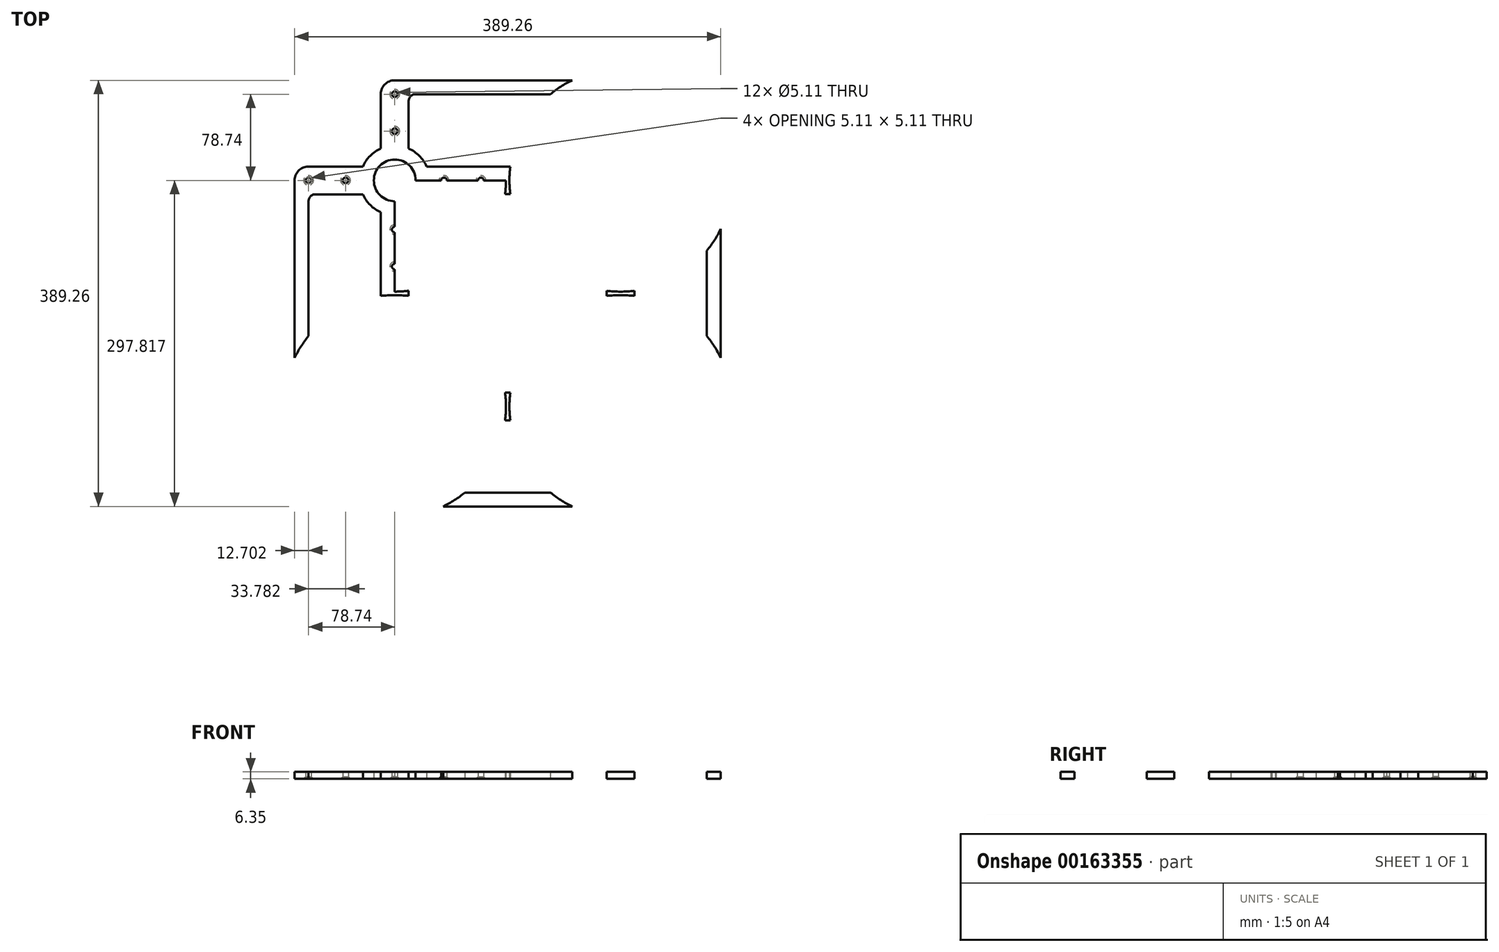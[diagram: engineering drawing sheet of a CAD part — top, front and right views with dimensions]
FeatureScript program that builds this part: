
annotation { "Feature Type Name" : "Feature", "Feature Type Description" : "" }
export const myFeature = defineFeature(function(context is Context, id is Id, definition is map)
    precondition{}
    {
        {
            var Q0;
            Q0=qCreatedBy(makeId("Top.planeOp"),FACE);
            var sketch = newSketch(context, id + "F0", { "sketchPlane" : qUnion([Q0])});
            skLineSegment(sketch, "E0.bottom", {"start": v(103.19, -103.19) * mm, "end": v(-103.19, -103.19) * mm});
            skLineSegment(sketch, "E0.top", {"start": v(103.19, 103.19) * mm, "end": v(-103.19, 103.19) * mm});
            skLineSegment(sketch, "E0.left", {"start": v(103.19, -103.19) * mm, "end": v(103.19, 103.19) * mm});
            skLineSegment(sketch, "E0.right", {"start": v(-103.19, -103.19) * mm, "end": v(-103.19, 90.53) * mm});
            skPoint(sketch, "E0.middle", {"position": v(0, 0) * mm});
            skCircle(sketch, "E1", {"center": v(-103.19, 103.19) * mm, "radius": 101.6 * mm});
            skCircle(sketch, "E2", {"center": v(103.19, 103.19) * mm, "radius": 101.6 * mm});
            skCircle(sketch, "E3", {"center": v(103.19, -103.19) * mm, "radius": 101.6 * mm});
            skCircle(sketch, "E4", {"center": v(-103.19, -103.19) * mm, "radius": 101.6 * mm});
            skLineSegment(sketch, "E5", {"start": v(-103.19, 115.88) * mm, "end": v(-103.19, 148.15) * mm});
            skLineSegment(sketch, "E6", {"start": v(-103.19, 148.15) * mm, "end": v(-103.19, 181.93) * mm});
            skLineSegment(sketch, "E7", {"start": v(-103.19, 103.19) * mm, "end": v(-58.23, 103.19) * mm});
            skLineSegment(sketch, "E8", {"start": v(-58.23, 103.19) * mm, "end": v(-24.45, 103.19) * mm});
            skLineSegment(sketch, "E9", {"start": v(-103.19, 90.53) * mm, "end": v(-103.19, 58.23) * mm});
            skLineSegment(sketch, "E10", {"start": v(-103.19, 58.23) * mm, "end": v(-103.19, 24.45) * mm});
            skLineSegment(sketch, "E11", {"start": v(-103.19, 103.19) * mm, "end": v(-148.15, 103.19) * mm});
            skLineSegment(sketch, "E12", {"start": v(-148.15, 103.19) * mm, "end": v(-181.93, 103.19) * mm});
            skLineSegment(sketch, "E13.MirrorCS", {"start": v(103.19, 103.19) * mm, "end": v(103.19, 58.23) * mm});
            skLineSegment(sketch, "E14.MirrorCS", {"start": v(58.23, 103.19) * mm, "end": v(24.45, 103.19) * mm});
            skLineSegment(sketch, "E15.MirrorCS", {"start": v(103.19, 103.19) * mm, "end": v(58.23, 103.19) * mm});
            skLineSegment(sketch, "E16.MirrorCS", {"start": v(148.15, 103.19) * mm, "end": v(181.93, 103.19) * mm});
            skLineSegment(sketch, "E17.MirrorCS", {"start": v(103.19, 103.19) * mm, "end": v(148.15, 103.19) * mm});
            skLineSegment(sketch, "E18.MirrorCS", {"start": v(103.19, 58.23) * mm, "end": v(103.19, 24.45) * mm});
            skLineSegment(sketch, "E19.MirrorCS", {"start": v(103.19, 103.19) * mm, "end": v(103.19, 148.15) * mm});
            skLineSegment(sketch, "E20.MirrorCS", {"start": v(103.19, 148.15) * mm, "end": v(103.19, 181.93) * mm});
            skLineSegment(sketch, "E21.MirrorCS", {"start": v(-103.19, -103.19) * mm, "end": v(-103.19, -58.23) * mm});
            skLineSegment(sketch, "E22.MirrorCS", {"start": v(-58.23, -103.19) * mm, "end": v(-24.45, -103.19) * mm});
            skLineSegment(sketch, "E23.MirrorCS", {"start": v(-103.19, -103.19) * mm, "end": v(-58.23, -103.19) * mm});
            skLineSegment(sketch, "E24.MirrorCS", {"start": v(-103.19, -148.15) * mm, "end": v(-103.19, -181.93) * mm});
            skLineSegment(sketch, "E25.MirrorCS", {"start": v(-103.19, -103.19) * mm, "end": v(-103.19, -148.15) * mm});
            skLineSegment(sketch, "E26.MirrorCS", {"start": v(-148.15, -103.19) * mm, "end": v(-181.93, -103.19) * mm});
            skLineSegment(sketch, "E27.MirrorCS", {"start": v(-103.19, -103.19) * mm, "end": v(-148.15, -103.19) * mm});
            skLineSegment(sketch, "E28.MirrorCS", {"start": v(-103.19, -58.23) * mm, "end": v(-103.19, -24.45) * mm});
            skLineSegment(sketch, "E29.MirrorCS", {"start": v(148.15, -103.19) * mm, "end": v(181.93, -103.19) * mm});
            skLineSegment(sketch, "E30.MirrorCS", {"start": v(103.19, -103.19) * mm, "end": v(103.19, -58.23) * mm});
            skLineSegment(sketch, "E31.MirrorCS", {"start": v(103.19, -103.19) * mm, "end": v(148.15, -103.19) * mm});
            skLineSegment(sketch, "E32.MirrorCS", {"start": v(103.19, -103.19) * mm, "end": v(58.23, -103.19) * mm});
            skLineSegment(sketch, "E33.MirrorCS", {"start": v(103.19, -58.23) * mm, "end": v(103.19, -24.45) * mm});
            skLineSegment(sketch, "E34.MirrorCS", {"start": v(103.19, -103.19) * mm, "end": v(103.19, -148.15) * mm});
            skLineSegment(sketch, "E35.MirrorCS", {"start": v(58.23, -103.19) * mm, "end": v(24.45, -103.19) * mm});
            skLineSegment(sketch, "E36.MirrorCS", {"start": v(103.19, -148.15) * mm, "end": v(103.19, -181.93) * mm});
            skLineSegment(sketch, "E37", {"start": v(-181.93, 90.49) * mm, "end": v(-181.93, 90.49) * mm});
            skArc(sketch, "E38", {"start": v(-103.19, 194.63) * mm, "mid": v(-112.17, 190.9) * mm, "end": v(-115.89, 181.93) * mm});
            skLineSegment(sketch, "E39", {"start": v(-103.19, 103.19) * mm, "end": v(-115.89, 103.19) * mm});
            skPoint(sketch, "E39.endSnap0", {"position": v(-125.67, 103.19) * mm});
            skLineSegment(sketch, "E40", {"start": v(-115.89, 74.09) * mm, "end": v(-115.89, -2.38) * mm});
            skLineSegment(sketch, "E41", {"start": v(-115.89, -2.38) * mm, "end": v(-115.89, 74.09) * mm});
            skLineSegment(sketch, "E42", {"start": v(-90.52, 175.58) * mm, "end": v(-90.52, 132.3) * mm});
            skLineSegment(sketch, "E43", {"start": v(-182.34, 115.88) * mm, "end": v(-132.29, 115.88) * mm});
            skLineSegment(sketch, "E44.trimOffspring", {"start": v(-2.38, 90.53) * mm, "end": v(2.38, 90.53) * mm});
            skLineSegment(sketch, "E45.trimOffspring", {"start": v(-74.09, 115.88) * mm, "end": v(2.38, 115.88) * mm});
            skLineSegment(sketch, "E46.trimOffspring", {"start": v(-115.89, 132.29) * mm, "end": v(-115.89, 181.93) * mm});
            skPoint(sketch, "E47.visualSharp", {"position": v(-115.89, 115.88) * mm});
            skPoint(sketch, "E48.visualSharp", {"position": v(-90.52, 115.88) * mm});
            skPoint(sketch, "E49.visualSharp", {"position": v(-115.89, 90.53) * mm});
            skPoint(sketch, "E50.visualSharp", {"position": v(-149.1, 90.53) * mm});
            skLineSegment(sketch, "E51", {"start": v(-74.07, 90.53) * mm, "end": v(2.38, 90.53) * mm});
            skLineSegment(sketch, "E52.trimOffspring", {"start": v(-90.52, 74.07) * mm, "end": v(-90.52, -2.38) * mm});
            skPoint(sketch, "E53.visualSharp", {"position": v(-90.52, 90.53) * mm});
            skLineSegment(sketch, "E54", {"start": v(-132.29, 90.49) * mm, "end": v(-175.58, 90.49) * mm});
            skLineSegment(sketch, "E55", {"start": v(-181.93, 84.14) * mm, "end": v(-181.93, -38.98) * mm});
            skLineSegment(sketch, "E56", {"start": v(-181.93, -38.98) * mm, "end": v(-194.63, -38.98) * mm});
            skLineSegment(sketch, "E57", {"start": v(-194.63, -38.98) * mm, "end": v(-194.63, 103.19) * mm});
            skLineSegment(sketch, "E58", {"start": v(-84.17, 181.93) * mm, "end": v(38.98, 181.93) * mm});
            skLineSegment(sketch, "E59", {"start": v(38.98, 181.93) * mm, "end": v(38.98, 194.63) * mm});
            skLineSegment(sketch, "E60", {"start": v(38.98, 194.63) * mm, "end": v(-103.19, 194.63) * mm});
            skArc(sketch, "E61.trimOffspring", {"start": v(-181.52, 115.88) * mm, "mid": v(-190.76, 112.31) * mm, "end": v(-194.63, 103.19) * mm});
            skPoint(sketch, "E62.visualSharp", {"position": v(-181.93, 90.49) * mm});
            skArc(sketch, "E62.filletArc", {"start": v(-175.58, 90.49) * mm, "mid": v(-180.07, 88.63) * mm, "end": v(-181.93, 84.14) * mm});
            skPoint(sketch, "E63.visualSharp", {"position": v(-90.52, 181.93) * mm});
            skArc(sketch, "E63.filletArc", {"start": v(-84.17, 181.93) * mm, "mid": v(-88.66, 180.07) * mm, "end": v(-90.52, 175.58) * mm});
            skLineSegment(sketch, "E64.MirrorCS", {"start": v(90.52, 74.07) * mm, "end": v(90.52, -2.38) * mm});
            skLineSegment(sketch, "E65.MirrorCS", {"start": v(74.07, 90.53) * mm, "end": v(-2.38, 90.53) * mm});
            skLineSegment(sketch, "E66.MirrorCS", {"start": v(74.09, 115.88) * mm, "end": v(-2.38, 115.88) * mm});
            skLineSegment(sketch, "E67.MirrorCS", {"start": v(90.52, 175.58) * mm, "end": v(90.52, 132.3) * mm});
            skLineSegment(sketch, "E68.MirrorCS", {"start": v(115.89, 132.29) * mm, "end": v(115.89, 181.93) * mm});
            skLineSegment(sketch, "E69.MirrorCS", {"start": v(115.89, -2.38) * mm, "end": v(115.89, 74.09) * mm});
            skLineSegment(sketch, "E70.MirrorCS", {"start": v(132.29, 90.49) * mm, "end": v(175.58, 90.49) * mm});
            skLineSegment(sketch, "E71.MirrorCS", {"start": v(182.34, 115.88) * mm, "end": v(132.29, 115.88) * mm});
            skArc(sketch, "E72.MirrorCS", {"start": v(175.58, 90.49) * mm, "mid": v(180.07, 88.63) * mm, "end": v(181.93, 84.14) * mm});
            skLineSegment(sketch, "E73.MirrorCS", {"start": v(181.93, 84.14) * mm, "end": v(181.93, -38.98) * mm});
            skLineSegment(sketch, "E74.MirrorCS", {"start": v(194.63, -38.98) * mm, "end": v(194.63, 103.19) * mm});
            skArc(sketch, "E75.MirrorCS", {"start": v(181.52, 115.88) * mm, "mid": v(190.76, 112.31) * mm, "end": v(194.63, 103.19) * mm});
            skLineSegment(sketch, "E76.MirrorCS", {"start": v(-38.98, 194.63) * mm, "end": v(103.19, 194.63) * mm});
            skLineSegment(sketch, "E77.MirrorCS", {"start": v(84.17, 181.93) * mm, "end": v(-38.98, 181.93) * mm});
            skArc(sketch, "E78.MirrorCS", {"start": v(84.17, 181.93) * mm, "mid": v(88.66, 180.07) * mm, "end": v(90.52, 175.58) * mm});
            skArc(sketch, "E79.MirrorCS", {"start": v(103.19, 194.63) * mm, "mid": v(112.17, 190.9) * mm, "end": v(115.89, 181.93) * mm});
            skLineSegment(sketch, "E80.MirrorCS", {"start": v(-182.34, -115.88) * mm, "end": v(-132.29, -115.88) * mm});
            skArc(sketch, "E81.MirrorCS", {"start": v(-181.52, -115.88) * mm, "mid": v(-190.76, -112.31) * mm, "end": v(-194.63, -103.19) * mm});
            skLineSegment(sketch, "E82.MirrorCS", {"start": v(-194.63, 38.98) * mm, "end": v(-194.63, -103.19) * mm});
            skLineSegment(sketch, "E83.MirrorCS", {"start": v(-181.93, -84.14) * mm, "end": v(-181.93, 38.98) * mm});
            skArc(sketch, "E84.MirrorCS", {"start": v(-175.58, -90.49) * mm, "mid": v(-180.07, -88.63) * mm, "end": v(-181.93, -84.14) * mm});
            skLineSegment(sketch, "E85.MirrorCS", {"start": v(-132.29, -90.49) * mm, "end": v(-175.58, -90.49) * mm});
            skLineSegment(sketch, "E86.MirrorCS", {"start": v(-115.89, 2.38) * mm, "end": v(-115.89, -74.09) * mm});
            skLineSegment(sketch, "E87.MirrorCS", {"start": v(-90.52, -74.07) * mm, "end": v(-90.52, 2.38) * mm});
            skLineSegment(sketch, "E88.MirrorCS", {"start": v(-74.07, -90.53) * mm, "end": v(2.38, -90.53) * mm});
            skLineSegment(sketch, "E89.MirrorCS", {"start": v(-74.09, -115.88) * mm, "end": v(2.38, -115.88) * mm});
            skLineSegment(sketch, "E90.MirrorCS", {"start": v(-90.52, -175.58) * mm, "end": v(-90.52, -132.3) * mm});
            skLineSegment(sketch, "E91.MirrorCS", {"start": v(-115.89, -132.29) * mm, "end": v(-115.89, -181.93) * mm});
            skArc(sketch, "E92.MirrorCS", {"start": v(-103.19, -194.63) * mm, "mid": v(-112.17, -190.9) * mm, "end": v(-115.89, -181.93) * mm});
            skLineSegment(sketch, "E93.MirrorCS", {"start": v(38.98, -194.63) * mm, "end": v(-103.19, -194.63) * mm});
            skLineSegment(sketch, "E94.MirrorCS", {"start": v(-84.17, -181.93) * mm, "end": v(38.98, -181.93) * mm});
            skArc(sketch, "E95.MirrorCS", {"start": v(-84.17, -181.93) * mm, "mid": v(-88.66, -180.07) * mm, "end": v(-90.52, -175.58) * mm});
            skLineSegment(sketch, "E96.MirrorCS", {"start": v(115.89, -132.29) * mm, "end": v(115.89, -181.93) * mm});
            skArc(sketch, "E97.MirrorCS", {"start": v(103.19, -194.63) * mm, "mid": v(112.17, -190.9) * mm, "end": v(115.89, -181.93) * mm});
            skArc(sketch, "E98.MirrorCS", {"start": v(84.17, -181.93) * mm, "mid": v(88.66, -180.07) * mm, "end": v(90.52, -175.58) * mm});
            skLineSegment(sketch, "E99.MirrorCS", {"start": v(90.52, -175.58) * mm, "end": v(90.52, -132.3) * mm});
            skLineSegment(sketch, "E100.MirrorCS", {"start": v(74.07, -90.53) * mm, "end": v(-2.38, -90.53) * mm});
            skLineSegment(sketch, "E101.MirrorCS", {"start": v(74.09, -115.88) * mm, "end": v(-2.38, -115.88) * mm});
            skLineSegment(sketch, "E102.MirrorCS", {"start": v(90.52, -74.07) * mm, "end": v(90.52, 2.38) * mm});
            skLineSegment(sketch, "E103.MirrorCS", {"start": v(132.29, -90.49) * mm, "end": v(175.58, -90.49) * mm});
            skArc(sketch, "E104.MirrorCS", {"start": v(175.58, -90.49) * mm, "mid": v(180.07, -88.63) * mm, "end": v(181.93, -84.14) * mm});
            skArc(sketch, "E105.MirrorCS", {"start": v(181.52, -115.88) * mm, "mid": v(190.76, -112.31) * mm, "end": v(194.63, -103.19) * mm});
            skLineSegment(sketch, "E106.MirrorCS", {"start": v(194.63, 38.98) * mm, "end": v(194.63, -103.19) * mm});
            skLineSegment(sketch, "E107.MirrorCS", {"start": v(181.93, -84.14) * mm, "end": v(181.93, 38.98) * mm});
            skLineSegment(sketch, "E108.MirrorCS", {"start": v(182.34, -115.88) * mm, "end": v(132.29, -115.88) * mm});
            skLineSegment(sketch, "E109.MirrorCS", {"start": v(-38.98, -194.63) * mm, "end": v(103.19, -194.63) * mm});
            skLineSegment(sketch, "E110.MirrorCS", {"start": v(84.17, -181.93) * mm, "end": v(-38.98, -181.93) * mm});
            skLineSegment(sketch, "E111.MirrorCS", {"start": v(115.89, 2.38) * mm, "end": v(115.89, -74.09) * mm});
            skCircle(sketch, "E112", {"center": v(-103.19, 103.19) * mm, "radius": 19.05 * mm});
            skArc(sketch, "E113", {"start": v(-132.29, 90.49) * mm, "mid": v(-125.64, 80.74) * mm, "end": v(-115.89, 74.09) * mm});
            skCircle(sketch, "E114", {"center": v(103.19, 103.19) * mm, "radius": 19.05 * mm});
            skArc(sketch, "E115", {"start": v(74.07, 90.53) * mm, "mid": v(80.73, 80.74) * mm, "end": v(90.52, 74.07) * mm});
            skCircle(sketch, "E116", {"center": v(-103.19, -103.19) * mm, "radius": 19.05 * mm});
            skArc(sketch, "E117", {"start": v(-132.29, -115.88) * mm, "mid": v(-125.64, -125.64) * mm, "end": v(-115.89, -132.29) * mm});
            skArc(sketch, "E118", {"start": v(74.09, -115.88) * mm, "mid": v(80.75, -125.65) * mm, "end": v(90.52, -132.3) * mm});
            skPoint(sketch, "E47.filletArc.start.orphan", {"position": v(-122.24, 115.88) * mm});
            skPoint(sketch, "E119.orphan", {"position": v(-115.89, 122.23) * mm});
            skPoint(sketch, "E48.filletArc.start.orphan", {"position": v(-90.52, 122.23) * mm});
            skPoint(sketch, "E120.orphan", {"position": v(-84.17, 115.88) * mm});
            skPoint(sketch, "E53.filletArc.start.orphan", {"position": v(-84.17, 90.53) * mm});
            skPoint(sketch, "E121.orphan", {"position": v(-90.52, 84.18) * mm});
            skPoint(sketch, "E122.orphan", {"position": v(-121.7, 90.49) * mm});
            skArc(sketch, "E123.trimOffspring", {"start": v(-115.89, 132.29) * mm, "mid": v(-125.64, 125.64) * mm, "end": v(-132.29, 115.88) * mm});
            skArc(sketch, "E124.trimOffspring", {"start": v(-74.09, 115.88) * mm, "mid": v(-80.75, 125.65) * mm, "end": v(-90.52, 132.3) * mm});
            skArc(sketch, "E125.trimOffspring", {"start": v(-90.52, 74.07) * mm, "mid": v(-80.73, 80.74) * mm, "end": v(-74.07, 90.53) * mm});
            skPoint(sketch, "E126.orphan", {"position": v(-115.89, 84.16) * mm});
            skPoint(sketch, "E127.orphan", {"position": v(90.52, 122.23) * mm});
            skPoint(sketch, "E128.MirrorCS.end.orphan", {"position": v(84.17, 115.88) * mm});
            skPoint(sketch, "E129.orphan", {"position": v(115.89, 122.23) * mm});
            skPoint(sketch, "E130.MirrorCS.start.orphan", {"position": v(122.24, 115.88) * mm});
            skPoint(sketch, "E131.orphan", {"position": v(121.7, 90.49) * mm});
            skPoint(sketch, "E132.orphan", {"position": v(115.89, 84.16) * mm});
            skPoint(sketch, "E133.orphan", {"position": v(84.17, 90.53) * mm});
            skPoint(sketch, "E134.MirrorCS.end.orphan", {"position": v(90.52, 84.18) * mm});
            skArc(sketch, "E135.trimOffspring", {"start": v(90.52, 132.3) * mm, "mid": v(80.75, 125.65) * mm, "end": v(74.09, 115.88) * mm});
            skArc(sketch, "E136.trimOffspring", {"start": v(132.29, 115.88) * mm, "mid": v(125.64, 125.64) * mm, "end": v(115.89, 132.29) * mm});
            skArc(sketch, "E137.trimOffspring", {"start": v(115.89, 74.09) * mm, "mid": v(125.64, 80.74) * mm, "end": v(132.29, 90.49) * mm});
            skPoint(sketch, "E138.orphan", {"position": v(90.52, -84.18) * mm});
            skPoint(sketch, "E139.orphan", {"position": v(84.17, -90.53) * mm});
            skPoint(sketch, "E140.orphan", {"position": v(115.89, -84.16) * mm});
            skPoint(sketch, "E141.MirrorCS.end.orphan", {"position": v(121.7, -90.49) * mm});
            skPoint(sketch, "E142.orphan", {"position": v(122.24, -115.88) * mm});
            skPoint(sketch, "E143.MirrorCS.end.orphan", {"position": v(115.89, -122.23) * mm});
            skPoint(sketch, "E144.MirrorCS.end.orphan", {"position": v(84.17, -115.88) * mm});
            skPoint(sketch, "E144.MirrorCS.start.orphan", {"position": v(90.52, -122.23) * mm});
            skArc(sketch, "E145.trimOffspring", {"start": v(90.52, -74.07) * mm, "mid": v(80.73, -80.74) * mm, "end": v(74.07, -90.53) * mm});
            skArc(sketch, "E146.trimOffspring", {"start": v(132.29, -90.49) * mm, "mid": v(125.64, -80.74) * mm, "end": v(115.89, -74.09) * mm});
            skArc(sketch, "E147.trimOffspring", {"start": v(115.89, -132.29) * mm, "mid": v(125.64, -125.64) * mm, "end": v(132.29, -115.88) * mm});
            skCircle(sketch, "E148", {"center": v(103.19, -103.19) * mm, "radius": 19.05 * mm});
            skPoint(sketch, "E149.orphan", {"position": v(-121.7, -90.49) * mm});
            skPoint(sketch, "E150.orphan", {"position": v(-115.89, -84.16) * mm});
            skArc(sketch, "E151.trimOffspring", {"start": v(-115.89, -74.09) * mm, "mid": v(-125.64, -80.74) * mm, "end": v(-132.29, -90.49) * mm});
            skPoint(sketch, "E152.orphan", {"position": v(-90.52, -84.18) * mm});
            skPoint(sketch, "E153.MirrorCS.start.orphan", {"position": v(-84.17, -90.53) * mm});
            skArc(sketch, "E154.trimOffspring", {"start": v(-74.07, -90.53) * mm, "mid": v(-80.73, -80.74) * mm, "end": v(-90.52, -74.07) * mm});
            skPoint(sketch, "E155.orphan", {"position": v(-84.17, -115.88) * mm});
            skPoint(sketch, "E156.MirrorCS.start.orphan", {"position": v(-90.52, -122.23) * mm});
            skArc(sketch, "E157.trimOffspring", {"start": v(-90.52, -132.3) * mm, "mid": v(-80.75, -125.65) * mm, "end": v(-74.09, -115.88) * mm});
            skPoint(sketch, "E158.orphan", {"position": v(-115.89, -122.23) * mm});
            skPoint(sketch, "E159.MirrorCS.start.orphan", {"position": v(-122.24, -115.88) * mm});
            skSolve(sketch);
        }
        {
            var Q0;
            {var subQ8=sQuery(id+"F0.wireOp",EDGE,"E14.MirrorCS");Q0=makeQuery(id+"F0.imprint","IMPRINT",FACE,{"disambiguationData":[TD([[makeQuery(id+"F0.imprint","IMPRINT",EDGE,{"derivedFrom":subQ8}),-1.0]])]});}
            var Q1;
            {var subQ1=sQuery(id+"F0.wireOp",EDGE,"E14.MirrorCS");Q1=makeQuery(id+"F0.imprint","IMPRINT",FACE,{"disambiguationData":[TD([[makeQuery(id+"F0.imprint","IMPRINT",EDGE,{"derivedFrom":subQ1}),1.0]])]});}
            var Q2;
            {var subQ0=sQuery(id+"F0.wireOp",EDGE,"E106.MirrorCS");var subQ3=sQuery(id+"F0.wireOp",EDGE,"E3");var subQ4=makeQuery(id+"F0.imprint","INTERSECT",VERTEX,{"derivedFrom":[subQ3,subQ0]});Q2=makeQuery(id+"F0.imprint","IMPRINT",FACE,{"disambiguationData":[TD([[makeQuery(id+"F0.imprint","IMPRINT",EDGE,{"disambiguationData":[TD([[subQ4,-1.0]])],"derivedFrom":subQ3}),-1.0]])]});}
            var Q3;
            {var subQ0=sQuery(id+"F0.wireOp",EDGE,"E3");var subQ1=sQuery(id+"F0.wireOp",EDGE,"E0.left");var subQ2=makeQuery(id+"F0.imprint","INTERSECT",VERTEX,{"derivedFrom":[subQ1,subQ0]});Q3=makeQuery(id+"F0.imprint","IMPRINT",FACE,{"disambiguationData":[TD([[makeQuery(id+"F0.imprint","IMPRINT",EDGE,{"disambiguationData":[TD([[subQ2,-1.0]])],"derivedFrom":subQ1}),1.0]])]});}
            var Q4;
            {var subQ0=sQuery(id+"F0.wireOp",EDGE,"E3");var subQ1=sQuery(id+"F0.wireOp",EDGE,"E0.left");var subQ2=makeQuery(id+"F0.imprint","INTERSECT",VERTEX,{"derivedFrom":[subQ1,subQ0]});Q4=makeQuery(id+"F0.imprint","IMPRINT",FACE,{"disambiguationData":[TD([[makeQuery(id+"F0.imprint","IMPRINT",EDGE,{"disambiguationData":[TD([[subQ2,-1.0]])],"derivedFrom":subQ1}),-1.0]])]});}
            var Q5;
            {var subQ0=sQuery(id+"F0.wireOp",EDGE,"E109.MirrorCS");var subQ3=sQuery(id+"F0.wireOp",EDGE,"E3");var subQ4=makeQuery(id+"F0.imprint","INTERSECT",VERTEX,{"derivedFrom":[subQ3,subQ0]});Q5=makeQuery(id+"F0.imprint","IMPRINT",FACE,{"disambiguationData":[TD([[makeQuery(id+"F0.imprint","IMPRINT",EDGE,{"disambiguationData":[TD([[subQ4,1.0]])],"derivedFrom":subQ3}),-1.0]])]});}
            var Q6;
            {var subQ0=sQuery(id+"F0.wireOp",EDGE,"E3");var subQ1=sQuery(id+"F0.wireOp",EDGE,"E0.bottom");var subQ2=makeQuery(id+"F0.imprint","INTERSECT",VERTEX,{"derivedFrom":[subQ1,subQ0]});Q6=makeQuery(id+"F0.imprint","IMPRINT",FACE,{"disambiguationData":[TD([[makeQuery(id+"F0.imprint","IMPRINT",EDGE,{"disambiguationData":[TD([[subQ2,-1.0]])],"derivedFrom":subQ1}),-1.0]])]});}
            var Q7;
            {var subQ0=sQuery(id+"F0.wireOp",EDGE,"E3");var subQ1=sQuery(id+"F0.wireOp",EDGE,"E0.bottom");var subQ2=makeQuery(id+"F0.imprint","INTERSECT",VERTEX,{"derivedFrom":[subQ1,subQ0]});Q7=makeQuery(id+"F0.imprint","IMPRINT",FACE,{"disambiguationData":[TD([[makeQuery(id+"F0.imprint","IMPRINT",EDGE,{"disambiguationData":[TD([[subQ2,-1.0]])],"derivedFrom":subQ1}),1.0]])]});}
            var Q8;
            {var subQ0=sQuery(id+"F0.wireOp",EDGE,"E56");Q8=makeQuery(id+"F0.imprint","IMPRINT",FACE,{"disambiguationData":[TD([[makeQuery(id+"F0.imprint","IMPRINT",EDGE,{"derivedFrom":subQ0}),1.0]])]});}
            var Q9;
            {var subQ1=sQuery(id+"F0.wireOp",EDGE,"E56");Q9=makeQuery(id+"F0.imprint","IMPRINT",FACE,{"disambiguationData":[TD([[makeQuery(id+"F0.imprint","IMPRINT",EDGE,{"derivedFrom":subQ1}),-1.0]])]});}
            var Q10;
            {var subQ17=sQuery(id+"F0.wireOp",EDGE,"E38");Q10=makeQuery(id+"F0.imprint","IMPRINT",FACE,{"disambiguationData":[TD([[makeQuery(id+"F0.imprint","IMPRINT",EDGE,{"derivedFrom":subQ17}),1.0]])]});}
            var Q11;
            {var subQ0=sQuery(id+"F0.wireOp",EDGE,"E1");var subQ1=sQuery(id+"F0.wireOp",EDGE,"E0.right");var subQ2=makeQuery(id+"F0.imprint","INTERSECT",VERTEX,{"derivedFrom":[subQ1,subQ0]});Q11=makeQuery(id+"F0.imprint","IMPRINT",FACE,{"disambiguationData":[TD([[makeQuery(id+"F0.imprint","IMPRINT",EDGE,{"disambiguationData":[TD([[subQ2,1.0]])],"derivedFrom":subQ1}),1.0]])]});}
            var Q12;
            {var subQ0=sQuery(id+"F0.wireOp",EDGE,"E1");var subQ1=sQuery(id+"F0.wireOp",EDGE,"E0.right");var subQ2=makeQuery(id+"F0.imprint","INTERSECT",VERTEX,{"derivedFrom":[subQ1,subQ0]});Q12=makeQuery(id+"F0.imprint","IMPRINT",FACE,{"disambiguationData":[TD([[makeQuery(id+"F0.imprint","IMPRINT",EDGE,{"disambiguationData":[TD([[subQ2,1.0]])],"derivedFrom":subQ1}),-1.0]])]});}
            var Q13;
            {var subQ0=sQuery(id+"F0.wireOp",EDGE,"E1");var subQ1=sQuery(id+"F0.wireOp",EDGE,"E0.top");var subQ2=makeQuery(id+"F0.imprint","INTERSECT",VERTEX,{"derivedFrom":[subQ1,subQ0]});Q13=makeQuery(id+"F0.imprint","IMPRINT",FACE,{"disambiguationData":[TD([[makeQuery(id+"F0.imprint","IMPRINT",EDGE,{"disambiguationData":[TD([[subQ2,1.0]])],"derivedFrom":subQ1}),1.0]])]});}
            var Q14;
            {var subQ0=sQuery(id+"F0.wireOp",EDGE,"E1");var subQ1=sQuery(id+"F0.wireOp",EDGE,"E0.top");var subQ2=makeQuery(id+"F0.imprint","INTERSECT",VERTEX,{"derivedFrom":[subQ1,subQ0]});Q14=makeQuery(id+"F0.imprint","IMPRINT",FACE,{"disambiguationData":[TD([[makeQuery(id+"F0.imprint","IMPRINT",EDGE,{"disambiguationData":[TD([[subQ2,1.0]])],"derivedFrom":subQ1}),-1.0]])]});}
            var Q15;
            {var subQ1=sQuery(id+"F0.wireOp",EDGE,"E59");Q15=makeQuery(id+"F0.imprint","IMPRINT",FACE,{"disambiguationData":[TD([[makeQuery(id+"F0.imprint","IMPRINT",EDGE,{"derivedFrom":subQ1}),1.0]])]});}
            var Q16;
            {var subQ0=sQuery(id+"F0.wireOp",EDGE,"E59");Q16=makeQuery(id+"F0.imprint","IMPRINT",FACE,{"disambiguationData":[TD([[makeQuery(id+"F0.imprint","IMPRINT",EDGE,{"derivedFrom":subQ0}),-1.0]])]});}
            var Q17;
            {var subQ2=sQuery(id+"F0.wireOp",EDGE,"E8");Q17=makeQuery(id+"F0.imprint","IMPRINT",FACE,{"disambiguationData":[TD([[makeQuery(id+"F0.imprint","IMPRINT",EDGE,{"derivedFrom":subQ2}),-1.0]])]});}
            var Q18;
            {var subQ7=sQuery(id+"F0.wireOp",EDGE,"E33.MirrorCS");Q18=makeQuery(id+"F0.imprint","IMPRINT",FACE,{"disambiguationData":[TD([[makeQuery(id+"F0.imprint","IMPRINT",EDGE,{"derivedFrom":subQ7}),1.0]])]});}
            var Q19;
            {var subQ30=sQuery(id+"F0.wireOp",EDGE,"E33.MirrorCS");Q19=makeQuery(id+"F0.imprint","IMPRINT",FACE,{"disambiguationData":[TD([[makeQuery(id+"F0.imprint","IMPRINT",EDGE,{"derivedFrom":subQ30}),-1.0]])]});}
            var Q20;
            {var subQ5=sQuery(id+"F0.wireOp",EDGE,"E22.MirrorCS");Q20=makeQuery(id+"F0.imprint","IMPRINT",FACE,{"disambiguationData":[TD([[makeQuery(id+"F0.imprint","IMPRINT",EDGE,{"derivedFrom":subQ5}),1.0]])]});}
            var Q21;
            {var subQ21=sQuery(id+"F0.wireOp",EDGE,"E22.MirrorCS");Q21=makeQuery(id+"F0.imprint","IMPRINT",FACE,{"disambiguationData":[TD([[makeQuery(id+"F0.imprint","IMPRINT",EDGE,{"derivedFrom":subQ21}),-1.0]])]});}
            extrude(context, id + "F1", {"entities" : qUnion([Q0, Q1, Q2, Q3, Q4, Q5, Q6, Q7, Q8, Q9, Q10, Q11, Q12, Q13, Q14, Q15, Q16, Q17, Q18, Q19, Q20, Q21]), "depth" : 6.35 * mm});
        }
        {
            var Q0;
            Q0=sQuery(id+"F0.wireOp",VERTEX,"E6.end");
            var Q1;
            Q1=sQuery(id+"F0.wireOp",VERTEX,"E6.start");
            var Q2;
            Q2=sQuery(id+"F0.wireOp",VERTEX,"E10.start");
            var Q3;
            Q3=sQuery(id+"F0.wireOp",VERTEX,"E10.end");
            var Q4;
            Q4=sQuery(id+"F0.wireOp",VERTEX,"E8.start");
            var Q5;
            Q5=sQuery(id+"F0.wireOp",VERTEX,"E8.end");
            var Q6;
            Q6=sQuery(id+"F0.wireOp",VERTEX,"E12.start");
            var Q7;
            Q7=sQuery(id+"F0.wireOp",VERTEX,"E81.MirrorCS.center");
            var Q8;
            Q8=sQuery(id+"F0.wireOp",VERTEX,"E27.MirrorCS.end");
            var Q9;
            Q9=sQuery(id+"F0.wireOp",VERTEX,"E21.MirrorCS.end");
            var Q10;
            Q10=sQuery(id+"F0.wireOp",VERTEX,"E28.MirrorCS.end");
            var Q11;
            Q11=sQuery(id+"F0.wireOp",VERTEX,"E22.MirrorCS.start");
            var Q12;
            Q12=sQuery(id+"F0.wireOp",VERTEX,"E22.MirrorCS.end");
            var Q13;
            Q13=sQuery(id+"F0.wireOp",VERTEX,"E25.MirrorCS.end");
            var Q14;
            Q14=sQuery(id+"F0.wireOp",VERTEX,"E92.MirrorCS.center");
            var Q15;
            Q15=sQuery(id+"F0.wireOp",VERTEX,"E14.MirrorCS.end");
            var Q16;
            Q16=sQuery(id+"F0.wireOp",VERTEX,"E15.MirrorCS.end");
            var Q17;
            Q17=sQuery(id+"F0.wireOp",VERTEX,"E79.MirrorCS.center");
            var Q18;
            Q18=sQuery(id+"F0.wireOp",VERTEX,"E20.MirrorCS.start");
            var Q19;
            Q19=sQuery(id+"F0.wireOp",VERTEX,"E13.MirrorCS.end");
            var Q20;
            Q20=sQuery(id+"F0.wireOp",VERTEX,"E18.MirrorCS.end");
            var Q21;
            Q21=sQuery(id+"F0.wireOp",VERTEX,"E33.MirrorCS.end");
            var Q22;
            Q22=sQuery(id+"F0.wireOp",VERTEX,"E30.MirrorCS.end");
            var Q23;
            Q23=sQuery(id+"F0.wireOp",VERTEX,"E36.MirrorCS.start");
            var Q24;
            Q24=sQuery(id+"F0.wireOp",VERTEX,"E36.MirrorCS.end");
            var Q25;
            Q25=sQuery(id+"F0.wireOp",VERTEX,"E35.MirrorCS.start");
            var Q26;
            Q26=sQuery(id+"F0.wireOp",VERTEX,"E35.MirrorCS.end");
            var Q27;
            Q27=sQuery(id+"F0.wireOp",VERTEX,"E17.MirrorCS.end");
            var Q28;
            Q28=sQuery(id+"F0.wireOp",VERTEX,"E16.MirrorCS.end");
            var Q29;
            Q29=sQuery(id+"F0.wireOp",VERTEX,"E29.MirrorCS.end");
            var Q30;
            Q30=sQuery(id+"F0.wireOp",VERTEX,"E29.MirrorCS.start");
            var Q31;
            Q31=makeQuery(id+"F1.opExtrude","SWEPT_BODY",BODY,{"disambiguationData":[OSD([sQuery(id+"F0.wireOp",EDGE,"E38"),sQuery(id+"F0.wireOp",EDGE,"E41"),sQuery(id+"F0.wireOp",EDGE,"E42"),sQuery(id+"F0.wireOp",EDGE,"E43"),sQuery(id+"F0.wireOp",EDGE,"E45.trimOffspring"),sQuery(id+"F0.wireOp",EDGE,"E46.trimOffspring"),sQuery(id+"F0.wireOp",EDGE,"E47.filletArc"),sQuery(id+"F0.wireOp",EDGE,"E48.filletArc"),sQuery(id+"F0.wireOp",EDGE,"E49.filletArc"),sQuery(id+"F0.wireOp",EDGE,"E51"),sQuery(id+"F0.wireOp",EDGE,"E52.trimOffspring"),sQuery(id+"F0.wireOp",EDGE,"E53.filletArc"),sQuery(id+"F0.wireOp",EDGE,"E54"),sQuery(id+"F0.wireOp",EDGE,"E55"),sQuery(id+"F0.wireOp",EDGE,"E57"),sQuery(id+"F0.wireOp",EDGE,"E58"),sQuery(id+"F0.wireOp",EDGE,"E60"),sQuery(id+"F0.wireOp",EDGE,"E61.trimOffspring"),sQuery(id+"F0.wireOp",EDGE,"E62.filletArc"),sQuery(id+"F0.wireOp",EDGE,"E63.filletArc"),sQuery(id+"F0.wireOp",EDGE,"E64.MirrorCS"),sQuery(id+"F0.wireOp",EDGE,"E65.MirrorCS"),sQuery(id+"F0.wireOp",EDGE,"E134.MirrorCS"),sQuery(id+"F0.wireOp",EDGE,"E128.MirrorCS"),sQuery(id+"F0.wireOp",EDGE,"E66.MirrorCS"),sQuery(id+"F0.wireOp",EDGE,"E67.MirrorCS"),sQuery(id+"F0.wireOp",EDGE,"E130.MirrorCS"),sQuery(id+"F0.wireOp",EDGE,"E68.MirrorCS"),sQuery(id+"F0.wireOp",EDGE,"221127f1-edb8-49a0-b02f-fde569e683690.MirrorCS"),sQuery(id+"F0.wireOp",EDGE,"E69.MirrorCS"),sQuery(id+"F0.wireOp",EDGE,"E70.MirrorCS"),sQuery(id+"F0.wireOp",EDGE,"E71.MirrorCS"),sQuery(id+"F0.wireOp",EDGE,"E72.MirrorCS"),sQuery(id+"F0.wireOp",EDGE,"E73.MirrorCS"),sQuery(id+"F0.wireOp",EDGE,"E74.MirrorCS"),sQuery(id+"F0.wireOp",EDGE,"E75.MirrorCS"),sQuery(id+"F0.wireOp",EDGE,"E76.MirrorCS"),sQuery(id+"F0.wireOp",EDGE,"E77.MirrorCS"),sQuery(id+"F0.wireOp",EDGE,"E78.MirrorCS"),sQuery(id+"F0.wireOp",EDGE,"E79.MirrorCS"),sQuery(id+"F0.wireOp",EDGE,"E81.MirrorCS"),sQuery(id+"F0.wireOp",EDGE,"E82.MirrorCS"),sQuery(id+"F0.wireOp",EDGE,"E83.MirrorCS"),sQuery(id+"F0.wireOp",EDGE,"E84.MirrorCS"),sQuery(id+"F0.wireOp",EDGE,"E85.MirrorCS"),sQuery(id+"F0.wireOp",EDGE,"ed7aa3cc-8cbb-4a19-9fea-5913c3f469780.MirrorCS"),sQuery(id+"F0.wireOp",EDGE,"E86.MirrorCS"),sQuery(id+"F0.wireOp",EDGE,"E87.MirrorCS"),sQuery(id+"F0.wireOp",EDGE,"E153.MirrorCS"),sQuery(id+"F0.wireOp",EDGE,"E88.MirrorCS"),sQuery(id+"F0.wireOp",EDGE,"E89.MirrorCS"),sQuery(id+"F0.wireOp",EDGE,"E156.MirrorCS"),sQuery(id+"F0.wireOp",EDGE,"E90.MirrorCS"),sQuery(id+"F0.wireOp",EDGE,"E159.MirrorCS"),sQuery(id+"F0.wireOp",EDGE,"E91.MirrorCS"),sQuery(id+"F0.wireOp",EDGE,"E80.MirrorCS"),sQuery(id+"F0.wireOp",EDGE,"E92.MirrorCS"),sQuery(id+"F0.wireOp",EDGE,"E93.MirrorCS"),sQuery(id+"F0.wireOp",EDGE,"E94.MirrorCS"),sQuery(id+"F0.wireOp",EDGE,"E95.MirrorCS"),sQuery(id+"F0.wireOp",EDGE,"E96.MirrorCS"),sQuery(id+"F0.wireOp",EDGE,"E97.MirrorCS"),sQuery(id+"F0.wireOp",EDGE,"E98.MirrorCS"),sQuery(id+"F0.wireOp",EDGE,"E99.MirrorCS"),sQuery(id+"F0.wireOp",EDGE,"E144.MirrorCS"),sQuery(id+"F0.wireOp",EDGE,"E100.MirrorCS"),sQuery(id+"F0.wireOp",EDGE,"E101.MirrorCS"),sQuery(id+"F0.wireOp",EDGE,"E102.MirrorCS"),sQuery(id+"F0.wireOp",EDGE,"E103.MirrorCS"),sQuery(id+"F0.wireOp",EDGE,"E104.MirrorCS"),sQuery(id+"F0.wireOp",EDGE,"E105.MirrorCS"),sQuery(id+"F0.wireOp",EDGE,"E106.MirrorCS"),sQuery(id+"F0.wireOp",EDGE,"E107.MirrorCS"),sQuery(id+"F0.wireOp",EDGE,"E108.MirrorCS"),sQuery(id+"F0.wireOp",EDGE,"E109.MirrorCS"),sQuery(id+"F0.wireOp",EDGE,"E110.MirrorCS"),sQuery(id+"F0.wireOp",EDGE,"E111.MirrorCS"),sQuery(id+"F0.wireOp",EDGE,"2e292ab2-123e-4bfc-9dde-d1669920952b0.MirrorCS"),sQuery(id+"F0.wireOp",EDGE,"72ab86d4-7202-410a-954c-d74877c1e6720.MirrorCS"),sQuery(id+"F0.wireOp",EDGE,"E143.MirrorCS")])]});
            hole(context, id + "F2", {"style" : HoleStyle.C_SINK, "endStyle" : HoleEndStyle.BLIND, "oppositeDirection" : true, "holeDiameter" : 5.1 * mm, "cSinkDiameter" : 8.9 * mm, "cSinkAngle" : 90 * degree, "holeDepth" : 76.2 * mm, "locations" : qUnion([Q0, Q1, Q2, Q3, Q4, Q5, Q6, Q7, Q8, Q9, Q10, Q11, Q12, Q13, Q14, Q15, Q16, Q17, Q18, Q19, Q20, Q21, Q22, Q23, Q24, Q25, Q26, Q27, Q28, Q29, Q30]), "scope" : qUnion([Q31])});
        }
        {
            var Q0;
            Q0=sQuery(id+"F0.wireOp",VERTEX,"E12.end");
            var Q1;
            Q1=makeQuery(id+"F1.opExtrude","SWEPT_BODY",BODY,{"disambiguationData":[OSD([sQuery(id+"F0.wireOp",EDGE,"E38"),sQuery(id+"F0.wireOp",EDGE,"E41"),sQuery(id+"F0.wireOp",EDGE,"E42"),sQuery(id+"F0.wireOp",EDGE,"E43"),sQuery(id+"F0.wireOp",EDGE,"E45.trimOffspring"),sQuery(id+"F0.wireOp",EDGE,"E46.trimOffspring"),sQuery(id+"F0.wireOp",EDGE,"E47.filletArc"),sQuery(id+"F0.wireOp",EDGE,"E48.filletArc"),sQuery(id+"F0.wireOp",EDGE,"E49.filletArc"),sQuery(id+"F0.wireOp",EDGE,"E51"),sQuery(id+"F0.wireOp",EDGE,"E52.trimOffspring"),sQuery(id+"F0.wireOp",EDGE,"E53.filletArc"),sQuery(id+"F0.wireOp",EDGE,"E54"),sQuery(id+"F0.wireOp",EDGE,"E55"),sQuery(id+"F0.wireOp",EDGE,"E57"),sQuery(id+"F0.wireOp",EDGE,"E58"),sQuery(id+"F0.wireOp",EDGE,"E60"),sQuery(id+"F0.wireOp",EDGE,"E61.trimOffspring"),sQuery(id+"F0.wireOp",EDGE,"E62.filletArc"),sQuery(id+"F0.wireOp",EDGE,"E63.filletArc"),sQuery(id+"F0.wireOp",EDGE,"E64.MirrorCS"),sQuery(id+"F0.wireOp",EDGE,"E65.MirrorCS"),sQuery(id+"F0.wireOp",EDGE,"E134.MirrorCS"),sQuery(id+"F0.wireOp",EDGE,"E128.MirrorCS"),sQuery(id+"F0.wireOp",EDGE,"E66.MirrorCS"),sQuery(id+"F0.wireOp",EDGE,"E67.MirrorCS"),sQuery(id+"F0.wireOp",EDGE,"E130.MirrorCS"),sQuery(id+"F0.wireOp",EDGE,"E68.MirrorCS"),sQuery(id+"F0.wireOp",EDGE,"221127f1-edb8-49a0-b02f-fde569e683690.MirrorCS"),sQuery(id+"F0.wireOp",EDGE,"E69.MirrorCS"),sQuery(id+"F0.wireOp",EDGE,"E70.MirrorCS"),sQuery(id+"F0.wireOp",EDGE,"E71.MirrorCS"),sQuery(id+"F0.wireOp",EDGE,"E72.MirrorCS"),sQuery(id+"F0.wireOp",EDGE,"E73.MirrorCS"),sQuery(id+"F0.wireOp",EDGE,"E74.MirrorCS"),sQuery(id+"F0.wireOp",EDGE,"E75.MirrorCS"),sQuery(id+"F0.wireOp",EDGE,"E76.MirrorCS"),sQuery(id+"F0.wireOp",EDGE,"E77.MirrorCS"),sQuery(id+"F0.wireOp",EDGE,"E78.MirrorCS"),sQuery(id+"F0.wireOp",EDGE,"E79.MirrorCS"),sQuery(id+"F0.wireOp",EDGE,"E81.MirrorCS"),sQuery(id+"F0.wireOp",EDGE,"E82.MirrorCS"),sQuery(id+"F0.wireOp",EDGE,"E83.MirrorCS"),sQuery(id+"F0.wireOp",EDGE,"E84.MirrorCS"),sQuery(id+"F0.wireOp",EDGE,"E85.MirrorCS"),sQuery(id+"F0.wireOp",EDGE,"ed7aa3cc-8cbb-4a19-9fea-5913c3f469780.MirrorCS"),sQuery(id+"F0.wireOp",EDGE,"E86.MirrorCS"),sQuery(id+"F0.wireOp",EDGE,"E87.MirrorCS"),sQuery(id+"F0.wireOp",EDGE,"E153.MirrorCS"),sQuery(id+"F0.wireOp",EDGE,"E88.MirrorCS"),sQuery(id+"F0.wireOp",EDGE,"E89.MirrorCS"),sQuery(id+"F0.wireOp",EDGE,"E156.MirrorCS"),sQuery(id+"F0.wireOp",EDGE,"E90.MirrorCS"),sQuery(id+"F0.wireOp",EDGE,"E159.MirrorCS"),sQuery(id+"F0.wireOp",EDGE,"E91.MirrorCS"),sQuery(id+"F0.wireOp",EDGE,"E80.MirrorCS"),sQuery(id+"F0.wireOp",EDGE,"E92.MirrorCS"),sQuery(id+"F0.wireOp",EDGE,"E93.MirrorCS"),sQuery(id+"F0.wireOp",EDGE,"E94.MirrorCS"),sQuery(id+"F0.wireOp",EDGE,"E95.MirrorCS"),sQuery(id+"F0.wireOp",EDGE,"E96.MirrorCS"),sQuery(id+"F0.wireOp",EDGE,"E97.MirrorCS"),sQuery(id+"F0.wireOp",EDGE,"E98.MirrorCS"),sQuery(id+"F0.wireOp",EDGE,"E99.MirrorCS"),sQuery(id+"F0.wireOp",EDGE,"E144.MirrorCS"),sQuery(id+"F0.wireOp",EDGE,"E100.MirrorCS"),sQuery(id+"F0.wireOp",EDGE,"E101.MirrorCS"),sQuery(id+"F0.wireOp",EDGE,"E102.MirrorCS"),sQuery(id+"F0.wireOp",EDGE,"E103.MirrorCS"),sQuery(id+"F0.wireOp",EDGE,"E104.MirrorCS"),sQuery(id+"F0.wireOp",EDGE,"E105.MirrorCS"),sQuery(id+"F0.wireOp",EDGE,"E106.MirrorCS"),sQuery(id+"F0.wireOp",EDGE,"E107.MirrorCS"),sQuery(id+"F0.wireOp",EDGE,"E108.MirrorCS"),sQuery(id+"F0.wireOp",EDGE,"E109.MirrorCS"),sQuery(id+"F0.wireOp",EDGE,"E110.MirrorCS"),sQuery(id+"F0.wireOp",EDGE,"E111.MirrorCS"),sQuery(id+"F0.wireOp",EDGE,"2e292ab2-123e-4bfc-9dde-d1669920952b0.MirrorCS"),sQuery(id+"F0.wireOp",EDGE,"72ab86d4-7202-410a-954c-d74877c1e6720.MirrorCS"),sQuery(id+"F0.wireOp",EDGE,"E143.MirrorCS")])]});
            hole(context, id + "F3", {"style" : HoleStyle.C_SINK, "endStyle" : HoleEndStyle.BLIND, "oppositeDirection" : true, "holeDiameter" : 5.1 * mm, "cSinkDiameter" : 8.9 * mm, "cSinkAngle" : 90 * degree, "holeDepth" : 76.2 * mm, "locations" : qUnion([Q0]), "scope" : qUnion([Q1])});
        }
    });
